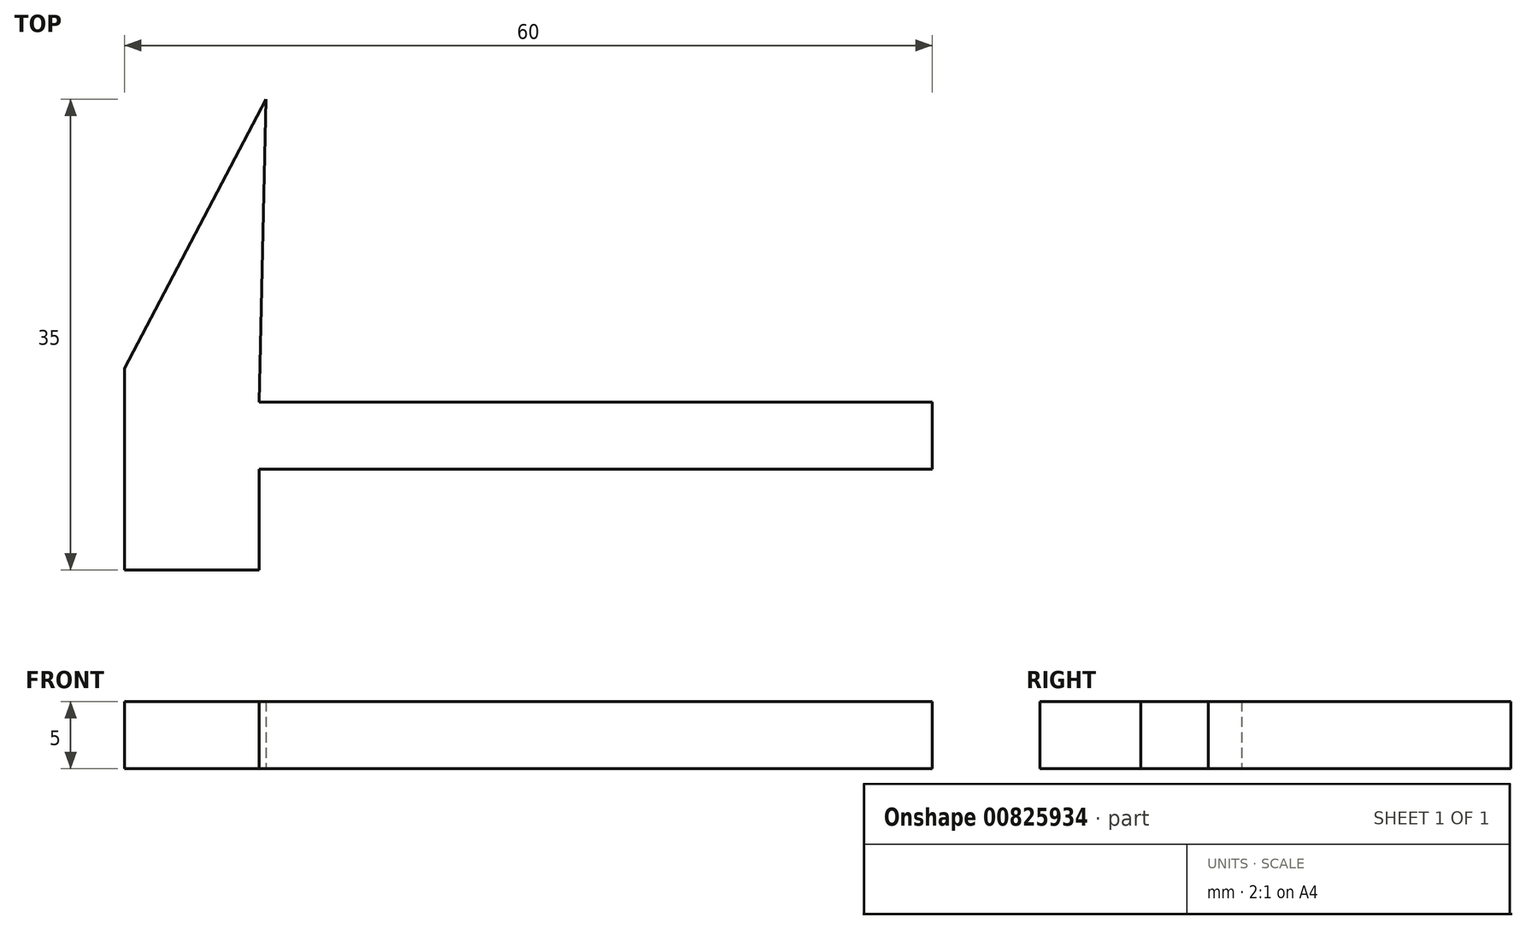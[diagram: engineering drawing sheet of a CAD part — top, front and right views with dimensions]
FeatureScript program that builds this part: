
annotation { "Feature Type Name" : "Feature", "Feature Type Description" : "" }
export const myFeature = defineFeature(function(context is Context, id is Id, definition is map)
    precondition{}
    {
        {
            var Q0;
            Q0=qCreatedBy(makeId("Top.planeOp"),FACE);
            var sketch = newSketch(context, id + "F0", { "sketchPlane" : qUnion([Q0])});
            skLineSegment(sketch, "E0.bottom", {"start": v(25, 2.5) * mm, "end": v(-25, 2.5) * mm});
            skLineSegment(sketch, "E0.top", {"start": v(25, -2.5) * mm, "end": v(-25, -2.5) * mm});
            skLineSegment(sketch, "E0.left", {"start": v(25, 2.5) * mm, "end": v(25, -2.5) * mm});
            skLineSegment(sketch, "E0.right", {"start": v(-25, 2.5) * mm, "end": v(-25, -2.5) * mm});
            skLineSegment(sketch, "E1", {"start": v(-35, 5) * mm, "end": v(-35, -2.5) * mm});
            skLineSegment(sketch, "E2", {"start": v(-35, -2.5) * mm, "end": v(-35, -2.5) * mm});
            skLineSegment(sketch, "E3", {"start": v(-35, -2.5) * mm, "end": v(-35, -10) * mm});
            skLineSegment(sketch, "E4", {"start": v(-35, -10) * mm, "end": v(-25, -10) * mm});
            skLineSegment(sketch, "E5", {"start": v(-25, -10) * mm, "end": v(-25, -2.5) * mm});
            skLineSegment(sketch, "E6", {"start": v(-25, -2.5) * mm, "end": v(-25, -2.5) * mm});
            skPoint(sketch, "E7.startSnap0", {"position": v(-25, -2.5) * mm});
            skLineSegment(sketch, "E8", {"start": v(-35, 5) * mm, "end": v(-24.5, 25) * mm});
            skLineSegment(sketch, "E9", {"start": v(-24.5, 25) * mm, "end": v(-25, 2.5) * mm});
            skLineSegment(sketch, "E10", {"start": v(-35, 5) * mm, "end": v(-24.94, 5) * mm});
            skSolve(sketch);
        }
        {
            var Q0;
            Q0=makeQuery(id+"F0.imprint","IMPRINT",FACE,{"disambiguationData":[TD([[makeQuery(id+"F0.imprint","IMPRINT",EDGE,{"derivedFrom":sQuery(id+"F0.wireOp",EDGE,"E0.right")}),-1.0]])]});
            var Q1;
            Q1=makeQuery(id+"F0.imprint","IMPRINT",FACE,{"disambiguationData":[TD([[makeQuery(id+"F0.imprint","IMPRINT",EDGE,{"derivedFrom":sQuery(id+"F0.wireOp",EDGE,"E0.bottom")}),1.0]])]});
            var Q2;
            {var subQ0=sQuery(id+"F0.wireOp",EDGE,"E8");Q2=makeQuery(id+"F0.imprint","IMPRINT",FACE,{"disambiguationData":[TD([[makeQuery(id+"F0.imprint","IMPRINT",EDGE,{"derivedFrom":subQ0}),-1.0]])]});}
            extrude(context, id + "F1", {"entities" : qUnion([Q0, Q1, Q2]), "depth" : 5 * mm, "offsetDistance" : 25 * mm});
        }
    });
